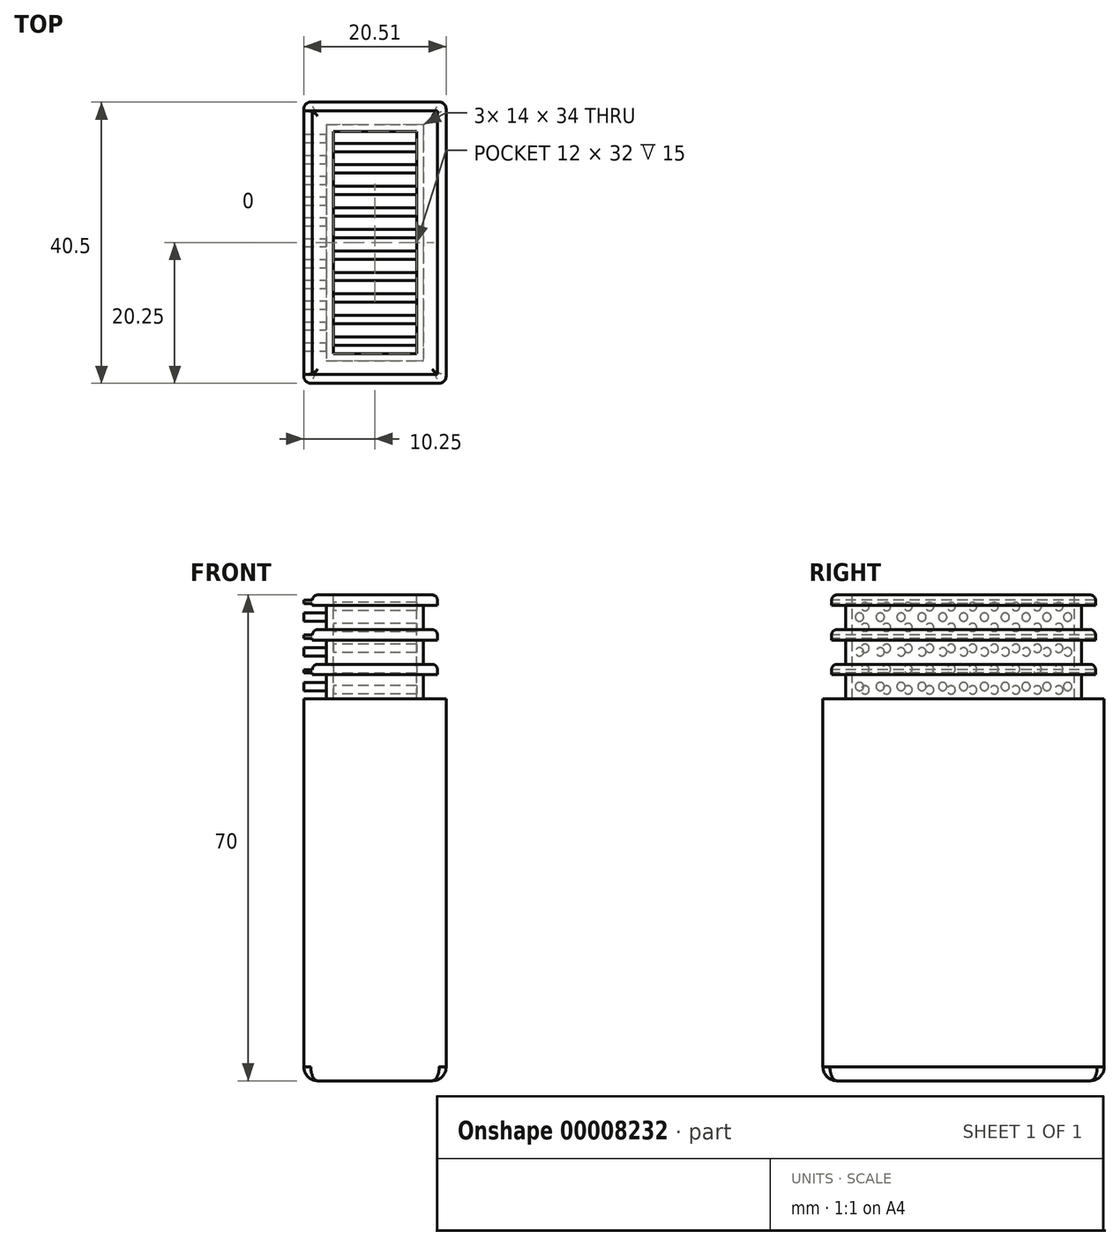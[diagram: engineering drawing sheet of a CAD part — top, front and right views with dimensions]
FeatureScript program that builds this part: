
annotation { "Feature Type Name" : "Feature", "Feature Type Description" : "" }
export const myFeature = defineFeature(function(context is Context, id is Id, definition is map)
    precondition{}
    {
        {
            var Q0;
            Q0=qCreatedBy(makeId("Top.planeOp"),FACE);
            var sketch = newSketch(context, id + "F0", { "sketchPlane" : qUnion([Q0])});
            skLineSegment(sketch, "E0.rect.bottom", {"start": v(10.25, -20.25) * mm, "end": v(-10.25, -20.25) * mm});
            skLineSegment(sketch, "E0.rect.top", {"start": v(10.25, 20.25) * mm, "end": v(-10.25, 20.25) * mm});
            skLineSegment(sketch, "E0.rect.left", {"start": v(10.25, -20.25) * mm, "end": v(10.25, 20.25) * mm});
            skLineSegment(sketch, "E0.rect.right", {"start": v(-10.25, -20.25) * mm, "end": v(-10.25, 20.25) * mm});
            skPoint(sketch, "E0.rect.middle", {"position": v(0, 0) * mm});
            skSolve(sketch);
        }
        {
            var Q0;
            Q0=makeQuery(id+"F0.imprint","IMPRINT",FACE,{"disambiguationData":[TD([[makeQuery(id+"F0.imprint","IMPRINT",EDGE,{"derivedFrom":sQuery(id+"F0.wireOp",EDGE,"E0.rect.bottom")}),-1.0]])]});
            extrude(context, id + "F1", {"entities" : qUnion([Q0]), "depth" : 53 * mm});
        }
        {
            var Q0;
            Q0=makeQuery(id+"F1.opExtrude","CAP_FACE",FACE,{"disambiguationData":[OSD([sQuery(id+"F0.wireOp",EDGE,"E0.rect.bottom"),sQuery(id+"F0.wireOp",EDGE,"E0.rect.top"),sQuery(id+"F0.wireOp",EDGE,"E0.rect.left"),sQuery(id+"F0.wireOp",EDGE,"E0.rect.right")])],"isStart":false});
            var sketch = newSketch(context, id + "F2", { "sketchPlane" : qUnion([Q0])});
            skLineSegment(sketch, "E1.bottom", {"start": v(-7, 17) * mm, "end": v(7, 17) * mm});
            skLineSegment(sketch, "E1.top", {"start": v(-7, -17) * mm, "end": v(7, -17) * mm});
            skLineSegment(sketch, "E1.left", {"start": v(-7, 17) * mm, "end": v(-7, -17) * mm});
            skLineSegment(sketch, "E1.right", {"start": v(7, 17) * mm, "end": v(7, -17) * mm});
            skSolve(sketch);
        }
        {
            var Q0;
            Q0 = qSketchRegion(id + "F2", true);
            extrude(context, id + "F3", {"entities" : qUnion([Q0]), "operationType" : NewBodyOperationType.ADD, "depth" : 3.5 * mm});
        }
        {
            var Q0;
            Q0=makeQuery(id+"F3.opExtrude","CAP_FACE",FACE,{"disambiguationData":[OSD([sQuery(id+"F2.wireOp",EDGE,"E1.bottom"),sQuery(id+"F2.wireOp",EDGE,"E1.top"),sQuery(id+"F2.wireOp",EDGE,"E1.left"),sQuery(id+"F2.wireOp",EDGE,"E1.right")])],"isStart":false});
            var sketch = newSketch(context, id + "F4", { "sketchPlane" : qUnion([Q0])});
            skLineSegment(sketch, "E2.bottom", {"start": v(-9, 19) * mm, "end": v(9, 19) * mm});
            skLineSegment(sketch, "E2.top", {"start": v(-9, -19) * mm, "end": v(9, -19) * mm});
            skLineSegment(sketch, "E2.left", {"start": v(-9, 19) * mm, "end": v(-9, -19) * mm});
            skLineSegment(sketch, "E2.right", {"start": v(9, 19) * mm, "end": v(9, -19) * mm});
            skSolve(sketch);
        }
        {
            var Q0;
            Q0 = qSketchRegion(id + "F4", true);
            extrude(context, id + "F5", {"entities" : qUnion([Q0]), "operationType" : NewBodyOperationType.ADD, "depth" : 1.5 * mm});
        }
        {
            var Q0;
            Q0=makeQuery(id+"F5.opExtrude","CAP_FACE",FACE,{"disambiguationData":[OSD([sQuery(id+"F4.wireOp",EDGE,"E2.bottom"),sQuery(id+"F4.wireOp",EDGE,"E2.top"),sQuery(id+"F4.wireOp",EDGE,"E2.left"),sQuery(id+"F4.wireOp",EDGE,"E2.right")])],"isStart":false});
            fillet(context, id + "F6", {"entities" : qUnion([Q0]), "radius" : 0.75 * mm, "tangentPropagation" : true, "allowEdgeOverflow" : false});
        }
        {
            var Q0;
            Q0=makeQuery(id+"F5.opExtrude","CAP_FACE",FACE,{"disambiguationData":[OSD([sQuery(id+"F4.wireOp",EDGE,"E2.bottom"),sQuery(id+"F4.wireOp",EDGE,"E2.top"),sQuery(id+"F4.wireOp",EDGE,"E2.left"),sQuery(id+"F4.wireOp",EDGE,"E2.right")])],"isStart":false});
            var sketch = newSketch(context, id + "F7", { "sketchPlane" : qUnion([Q0])});
            skLineSegment(sketch, "E3.rect.bottom", {"start": v(-7, -17) * mm, "end": v(7, -17) * mm});
            skLineSegment(sketch, "E3.rect.top", {"start": v(-7, 17) * mm, "end": v(7, 17) * mm});
            skLineSegment(sketch, "E3.rect.left", {"start": v(-7, -17) * mm, "end": v(-7, 17) * mm});
            skLineSegment(sketch, "E3.rect.right", {"start": v(7, -17) * mm, "end": v(7, 17) * mm});
            skPoint(sketch, "E3.rect.middle", {"position": v(0, 0) * mm});
            skSolve(sketch);
        }
        {
            var Q0;
            Q0 = qSketchRegion(id + "F7", true);
            extrude(context, id + "F8", {"entities" : qUnion([Q0]), "operationType" : NewBodyOperationType.ADD, "depth" : 3.5 * mm});
        }
        {
            var Q0;
            Q0=makeQuery(id+"F8.opExtrude","CAP_FACE",FACE,{"disambiguationData":[OSD([sQuery(id+"F7.wireOp",EDGE,"E3.rect.bottom"),sQuery(id+"F7.wireOp",EDGE,"E3.rect.top"),sQuery(id+"F7.wireOp",EDGE,"E3.rect.left"),sQuery(id+"F7.wireOp",EDGE,"E3.rect.right")])],"isStart":false});
            var sketch = newSketch(context, id + "F9", { "sketchPlane" : qUnion([Q0])});
            skLineSegment(sketch, "E4.bottom", {"start": v(-9, 19) * mm, "end": v(9, 19) * mm});
            skLineSegment(sketch, "E4.top", {"start": v(-9, -19) * mm, "end": v(9, -19) * mm});
            skLineSegment(sketch, "E4.left", {"start": v(-9, 19) * mm, "end": v(-9, -19) * mm});
            skLineSegment(sketch, "E4.right", {"start": v(9, 19) * mm, "end": v(9, -19) * mm});
            skSolve(sketch);
        }
        {
            var Q0;
            Q0 = qSketchRegion(id + "F9", true);
            extrude(context, id + "F10", {"entities" : qUnion([Q0]), "operationType" : NewBodyOperationType.ADD, "depth" : 1.5 * mm});
        }
        {
            var Q0;
            Q0=makeQuery(id+"F10.opExtrude","CAP_FACE",FACE,{"disambiguationData":[OSD([sQuery(id+"F9.wireOp",EDGE,"E4.bottom"),sQuery(id+"F9.wireOp",EDGE,"E4.top"),sQuery(id+"F9.wireOp",EDGE,"E4.left"),sQuery(id+"F9.wireOp",EDGE,"E4.right")])],"isStart":false});
            var sketch = newSketch(context, id + "F11", { "sketchPlane" : qUnion([Q0])});
            skLineSegment(sketch, "E5.bottom", {"start": v(-7, 17) * mm, "end": v(7, 17) * mm});
            skLineSegment(sketch, "E5.top", {"start": v(-7, -17) * mm, "end": v(7, -17) * mm});
            skLineSegment(sketch, "E5.left", {"start": v(-7, 17) * mm, "end": v(-7, -17) * mm});
            skLineSegment(sketch, "E5.right", {"start": v(7, 17) * mm, "end": v(7, -17) * mm});
            skSolve(sketch);
        }
        {
            var Q0;
            Q0 = qSketchRegion(id + "F11", true);
            extrude(context, id + "F12", {"entities" : qUnion([Q0]), "operationType" : NewBodyOperationType.ADD, "depth" : 3.5 * mm});
        }
        {
            var Q0;
            Q0=makeQuery(id+"F12.opExtrude","CAP_FACE",FACE,{"disambiguationData":[OSD([sQuery(id+"F11.wireOp",EDGE,"E5.bottom"),sQuery(id+"F11.wireOp",EDGE,"E5.top"),sQuery(id+"F11.wireOp",EDGE,"E5.left"),sQuery(id+"F11.wireOp",EDGE,"E5.right")])],"isStart":false});
            var sketch = newSketch(context, id + "F13", { "sketchPlane" : qUnion([Q0])});
            skLineSegment(sketch, "E6.bottom", {"start": v(-9, 19) * mm, "end": v(9, 19) * mm});
            skLineSegment(sketch, "E6.top", {"start": v(-9, -19) * mm, "end": v(9, -19) * mm});
            skLineSegment(sketch, "E6.left", {"start": v(-9, 19) * mm, "end": v(-9, -19) * mm});
            skLineSegment(sketch, "E6.right", {"start": v(9, 19) * mm, "end": v(9, -19) * mm});
            skSolve(sketch);
        }
        {
            var Q0;
            Q0=makeQuery(id+"F13.imprint","IMPRINT",FACE,{"disambiguationData":[TD([[makeQuery(id+"F13.imprint","IMPRINT",EDGE,{"derivedFrom":sQuery(id+"F13.wireOp",EDGE,"E6.bottom")}),-1.0]])]});
            var Q1;
            Q1=makeQuery(id+"F13.imprint","IMPRINT",FACE,{"disambiguationData":[TD([[makeQuery(id+"F13.imprint","IMPRINT",EDGE,{"derivedFrom":makeQuery(id+"F12.opExtrude","CAP_EDGE",EDGE,{"disambiguationData":[OSD([sQuery(id+"F11.wireOp",EDGE,"E5.bottom")])],"isStart":false})}),-1.0]])]});
            extrude(context, id + "F14", {"entities" : qUnion([Q0, Q1]), "operationType" : NewBodyOperationType.ADD, "depth" : 1.5 * mm});
        }
        {
            var Q0;
            Q0=makeQuery(id+"F10.opExtrude","CAP_EDGE",EDGE,{"disambiguationData":[OSD([sQuery(id+"F9.wireOp",EDGE,"E4.bottom")])],"isStart":false});
            var Q1;
            Q1=makeQuery(id+"F10.opExtrude","CAP_EDGE",EDGE,{"disambiguationData":[OSD([sQuery(id+"F9.wireOp",EDGE,"E4.left")])],"isStart":false});
            var Q2;
            Q2=makeQuery(id+"F10.opExtrude","CAP_EDGE",EDGE,{"disambiguationData":[OSD([sQuery(id+"F9.wireOp",EDGE,"E4.right")])],"isStart":false});
            var Q3;
            Q3=makeQuery(id+"F10.opExtrude","CAP_EDGE",EDGE,{"disambiguationData":[OSD([sQuery(id+"F9.wireOp",EDGE,"E4.top")])],"isStart":false});
            fillet(context, id + "F15", {"entities" : qUnion([Q0, Q1, Q2, Q3]), "radius" : 0.75 * mm, "tangentPropagation" : true, "allowEdgeOverflow" : false});
        }
        {
            var Q0;
            Q0=makeQuery(id+"F14.opExtrude","CAP_EDGE",EDGE,{"disambiguationData":[OSD([sQuery(id+"F13.wireOp",EDGE,"E6.left")])],"isStart":false});
            var Q1;
            Q1=makeQuery(id+"F14.opExtrude","CAP_EDGE",EDGE,{"disambiguationData":[OSD([sQuery(id+"F13.wireOp",EDGE,"E6.top")])],"isStart":false});
            var Q2;
            Q2=makeQuery(id+"F14.opExtrude","CAP_EDGE",EDGE,{"disambiguationData":[OSD([sQuery(id+"F13.wireOp",EDGE,"E6.right")])],"isStart":false});
            var Q3;
            Q3=makeQuery(id+"F14.opExtrude","CAP_EDGE",EDGE,{"disambiguationData":[OSD([sQuery(id+"F13.wireOp",EDGE,"E6.bottom")])],"isStart":false});
            fillet(context, id + "F16", {"entities" : qUnion([Q0, Q1, Q2, Q3]), "radius" : 0.75 * mm, "tangentPropagation" : true, "allowEdgeOverflow" : false});
        }
        {
            var Q0;
            Q0=makeQuery(id+"F14.opExtrude","CAP_FACE",FACE,{"disambiguationData":[OSD([sQuery(id+"F13.wireOp",EDGE,"E6.bottom"),sQuery(id+"F13.wireOp",EDGE,"E6.top"),sQuery(id+"F13.wireOp",EDGE,"E6.left"),sQuery(id+"F13.wireOp",EDGE,"E6.right")])],"isStart":false});
            var sketch = newSketch(context, id + "F17", { "sketchPlane" : qUnion([Q0])});
            skLineSegment(sketch, "E7.bottom", {"start": v(-6, 16) * mm, "end": v(6, 16) * mm});
            skLineSegment(sketch, "E7.top", {"start": v(-6, -16) * mm, "end": v(6, -16) * mm});
            skLineSegment(sketch, "E7.left", {"start": v(-6, 16) * mm, "end": v(-6, -16) * mm});
            skLineSegment(sketch, "E7.right", {"start": v(6, 16) * mm, "end": v(6, -16) * mm});
            skSolve(sketch);
        }
        {
            var Q0;
            Q0=makeQuery(id+"F17.imprint","IMPRINT",FACE,{"disambiguationData":[TD([[makeQuery(id+"F17.imprint","IMPRINT",EDGE,{"derivedFrom":sQuery(id+"F17.wireOp",EDGE,"E7.bottom")}),-1.0]])]});
            var Q1;
            Q1=makeQuery(id+"F1.opExtrude","CAP_FACE",FACE,{"disambiguationData":[OSD([sQuery(id+"F0.wireOp",EDGE,"E0.rect.bottom"),sQuery(id+"F0.wireOp",EDGE,"E0.rect.top"),sQuery(id+"F0.wireOp",EDGE,"E0.rect.left"),sQuery(id+"F0.wireOp",EDGE,"E0.rect.right")])],"isStart":false});
            extrude(context, id + "F18", {"entities" : qUnion([Q0]), "operationType" : NewBodyOperationType.REMOVE, "oppositeDirection" : true, "endBoundEntity" : qUnion([Q1]), "depth" : 15 * mm});
        }
        {
            var Q0;
            Q0=makeQuery(id+"F1.opExtrude","SWEPT_EDGE",EDGE,{"disambiguationData":[OSD([sQuery(id+"F0.wireOp",EDGE,"E0.rect.bottom"),sQuery(id+"F0.wireOp",EDGE,"E0.rect.left")])]});
            var Q1;
            Q1=makeQuery(id+"F1.opExtrude","SWEPT_EDGE",EDGE,{"disambiguationData":[OSD([sQuery(id+"F0.wireOp",EDGE,"E0.rect.top"),sQuery(id+"F0.wireOp",EDGE,"E0.rect.left")])]});
            var Q2;
            Q2=makeQuery(id+"F1.opExtrude","SWEPT_EDGE",EDGE,{"disambiguationData":[OSD([sQuery(id+"F0.wireOp",EDGE,"E0.rect.top"),sQuery(id+"F0.wireOp",EDGE,"E0.rect.right")])]});
            var Q3;
            Q3=makeQuery(id+"F1.opExtrude","SWEPT_EDGE",EDGE,{"disambiguationData":[OSD([sQuery(id+"F0.wireOp",EDGE,"E0.rect.bottom"),sQuery(id+"F0.wireOp",EDGE,"E0.rect.right")])]});
            fillet(context, id + "F19", {"entities" : qUnion([Q0, Q1, Q2, Q3]), "radius" : 1 * mm, "tangentPropagation" : true, "allowEdgeOverflow" : false});
        }
        {
            var Q0;
            Q0=makeQuery(id+"F1.opExtrude","CAP_FACE",FACE,{"disambiguationData":[OSD([sQuery(id+"F0.wireOp",EDGE,"E0.rect.bottom"),sQuery(id+"F0.wireOp",EDGE,"E0.rect.top"),sQuery(id+"F0.wireOp",EDGE,"E0.rect.left"),sQuery(id+"F0.wireOp",EDGE,"E0.rect.right")])],"isStart":true});
            var sketch = newSketch(context, id + "F20", { "sketchPlane" : qUnion([Q0])});
            skLineSegment(sketch, "E8.bottom", {"start": v(-7.25, 17.25) * mm, "end": v(-4.75, 17.25) * mm});
            skLineSegment(sketch, "E8.top", {"start": v(-7.25, 14.25) * mm, "end": v(-4.75, 14.25) * mm});
            skLineSegment(sketch, "E8.left", {"start": v(-7.25, 17.25) * mm, "end": v(-7.25, 14.25) * mm});
            skLineSegment(sketch, "E8.right", {"start": v(-4.75, 17.25) * mm, "end": v(-4.75, 14.25) * mm});
            skLineSegment(sketch, "E9.1.0.0", {"start": v(-3.25, 17.25) * mm, "end": v(-0.75, 17.25) * mm});
            skLineSegment(sketch, "E9.1.0.1", {"start": v(-0.75, 17.25) * mm, "end": v(-0.75, 14.25) * mm});
            skLineSegment(sketch, "E9.1.0.2", {"start": v(-3.25, 17.25) * mm, "end": v(-3.25, 14.25) * mm});
            skLineSegment(sketch, "E9.1.0.3", {"start": v(-3.25, 14.25) * mm, "end": v(-0.75, 14.25) * mm});
            skLineSegment(sketch, "E9.2.0.0", {"start": v(0.75, 17.25) * mm, "end": v(3.25, 17.25) * mm});
            skLineSegment(sketch, "E9.2.0.1", {"start": v(3.25, 17.25) * mm, "end": v(3.25, 14.25) * mm});
            skLineSegment(sketch, "E9.2.0.2", {"start": v(0.75, 17.25) * mm, "end": v(0.75, 14.25) * mm});
            skLineSegment(sketch, "E9.2.0.3", {"start": v(0.75, 14.25) * mm, "end": v(3.25, 14.25) * mm});
            skLineSegment(sketch, "E9.3.0.0", {"start": v(4.75, 17.25) * mm, "end": v(7.25, 17.25) * mm});
            skLineSegment(sketch, "E9.3.0.1", {"start": v(7.25, 17.25) * mm, "end": v(7.25, 14.25) * mm});
            skLineSegment(sketch, "E9.3.0.2", {"start": v(4.75, 17.25) * mm, "end": v(4.75, 14.25) * mm});
            skLineSegment(sketch, "E9.3.0.3", {"start": v(4.75, 14.25) * mm, "end": v(7.25, 14.25) * mm});
            skLineSegment(sketch, "E9.direction1", {"start": v(-7.25, 17.25) * mm, "end": v(-3.25, 17.25) * mm, "construction": true});
            skLineSegment(sketch, "E10.1.0.0", {"start": v(-7.24, 12.75) * mm, "end": v(-7.24, 9.75) * mm});
            skLineSegment(sketch, "E10.1.0.1", {"start": v(-3.24, 12.75) * mm, "end": v(-3.24, 9.75) * mm});
            skLineSegment(sketch, "E10.1.0.2", {"start": v(-3.24, 9.75) * mm, "end": v(-0.74, 9.75) * mm});
            skLineSegment(sketch, "E10.1.0.3", {"start": v(4.76, 9.75) * mm, "end": v(7.26, 9.75) * mm});
            skLineSegment(sketch, "E10.1.0.4", {"start": v(-7.24, 9.75) * mm, "end": v(-4.74, 9.75) * mm});
            skLineSegment(sketch, "E10.1.0.5", {"start": v(-7.24, 12.75) * mm, "end": v(-4.74, 12.75) * mm});
            skLineSegment(sketch, "E10.1.0.6", {"start": v(4.76, 12.75) * mm, "end": v(4.76, 9.75) * mm});
            skLineSegment(sketch, "E10.1.0.7", {"start": v(-0.74, 12.75) * mm, "end": v(-0.74, 9.75) * mm});
            skLineSegment(sketch, "E10.1.0.8", {"start": v(-7.24, 12.75) * mm, "end": v(-3.24, 12.75) * mm, "construction": true});
            skLineSegment(sketch, "E10.1.0.9", {"start": v(0.76, 9.75) * mm, "end": v(3.26, 9.75) * mm});
            skLineSegment(sketch, "E10.1.0.10", {"start": v(4.76, 12.75) * mm, "end": v(7.26, 12.75) * mm});
            skLineSegment(sketch, "E10.1.0.11", {"start": v(0.76, 12.75) * mm, "end": v(3.26, 12.75) * mm});
            skLineSegment(sketch, "E10.1.0.12", {"start": v(3.26, 12.75) * mm, "end": v(3.26, 9.75) * mm});
            skLineSegment(sketch, "E10.1.0.13", {"start": v(7.26, 12.75) * mm, "end": v(7.26, 9.75) * mm});
            skLineSegment(sketch, "E10.1.0.14", {"start": v(0.76, 12.75) * mm, "end": v(0.76, 9.75) * mm});
            skLineSegment(sketch, "E10.1.0.15", {"start": v(-3.24, 12.75) * mm, "end": v(-0.74, 12.75) * mm});
            skLineSegment(sketch, "E10.1.0.16", {"start": v(-4.74, 12.75) * mm, "end": v(-4.74, 9.75) * mm});
            skLineSegment(sketch, "E10.2.0.0", {"start": v(-7.22, 8.25) * mm, "end": v(-7.22, 5.25) * mm});
            skLineSegment(sketch, "E10.2.0.1", {"start": v(-3.22, 8.25) * mm, "end": v(-3.22, 5.25) * mm});
            skLineSegment(sketch, "E10.2.0.2", {"start": v(-3.22, 5.25) * mm, "end": v(-0.72, 5.25) * mm});
            skLineSegment(sketch, "E10.2.0.3", {"start": v(4.78, 5.25) * mm, "end": v(7.28, 5.25) * mm});
            skLineSegment(sketch, "E10.2.0.4", {"start": v(-7.22, 5.25) * mm, "end": v(-4.72, 5.25) * mm});
            skLineSegment(sketch, "E10.2.0.5", {"start": v(-7.22, 8.25) * mm, "end": v(-4.72, 8.25) * mm});
            skLineSegment(sketch, "E10.2.0.6", {"start": v(4.78, 8.25) * mm, "end": v(4.78, 5.25) * mm});
            skLineSegment(sketch, "E10.2.0.7", {"start": v(-0.72, 8.25) * mm, "end": v(-0.72, 5.25) * mm});
            skLineSegment(sketch, "E10.2.0.8", {"start": v(-7.22, 8.25) * mm, "end": v(-3.22, 8.25) * mm, "construction": true});
            skLineSegment(sketch, "E10.2.0.9", {"start": v(0.78, 5.25) * mm, "end": v(3.28, 5.25) * mm});
            skLineSegment(sketch, "E10.2.0.10", {"start": v(4.78, 8.25) * mm, "end": v(7.28, 8.25) * mm});
            skLineSegment(sketch, "E10.2.0.11", {"start": v(0.78, 8.25) * mm, "end": v(3.28, 8.25) * mm});
            skLineSegment(sketch, "E10.2.0.12", {"start": v(3.28, 8.25) * mm, "end": v(3.28, 5.25) * mm});
            skLineSegment(sketch, "E10.2.0.13", {"start": v(7.28, 8.25) * mm, "end": v(7.28, 5.25) * mm});
            skLineSegment(sketch, "E10.2.0.14", {"start": v(0.78, 8.25) * mm, "end": v(0.78, 5.25) * mm});
            skLineSegment(sketch, "E10.2.0.15", {"start": v(-3.22, 8.25) * mm, "end": v(-0.72, 8.25) * mm});
            skLineSegment(sketch, "E10.2.0.16", {"start": v(-4.72, 8.25) * mm, "end": v(-4.72, 5.25) * mm});
            skLineSegment(sketch, "E10.3.0.0", {"start": v(-7.21, 3.75) * mm, "end": v(-7.21, 0.75) * mm});
            skLineSegment(sketch, "E10.3.0.1", {"start": v(-3.21, 3.75) * mm, "end": v(-3.21, 0.75) * mm});
            skLineSegment(sketch, "E10.3.0.2", {"start": v(-3.21, 0.75) * mm, "end": v(-0.71, 0.75) * mm});
            skLineSegment(sketch, "E10.3.0.3", {"start": v(4.79, 0.75) * mm, "end": v(7.29, 0.75) * mm});
            skLineSegment(sketch, "E10.3.0.4", {"start": v(-7.21, 0.75) * mm, "end": v(-4.71, 0.75) * mm});
            skLineSegment(sketch, "E10.3.0.5", {"start": v(-7.21, 3.75) * mm, "end": v(-4.71, 3.75) * mm});
            skLineSegment(sketch, "E10.3.0.6", {"start": v(4.79, 3.75) * mm, "end": v(4.79, 0.75) * mm});
            skLineSegment(sketch, "E10.3.0.7", {"start": v(-0.71, 3.75) * mm, "end": v(-0.71, 0.75) * mm});
            skLineSegment(sketch, "E10.3.0.8", {"start": v(-7.21, 3.75) * mm, "end": v(-3.21, 3.75) * mm, "construction": true});
            skLineSegment(sketch, "E10.3.0.9", {"start": v(0.79, 0.75) * mm, "end": v(3.29, 0.75) * mm});
            skLineSegment(sketch, "E10.3.0.10", {"start": v(4.79, 3.75) * mm, "end": v(7.29, 3.75) * mm});
            skLineSegment(sketch, "E10.3.0.11", {"start": v(0.79, 3.75) * mm, "end": v(3.29, 3.75) * mm});
            skLineSegment(sketch, "E10.3.0.12", {"start": v(3.29, 3.75) * mm, "end": v(3.29, 0.75) * mm});
            skLineSegment(sketch, "E10.3.0.13", {"start": v(7.29, 3.75) * mm, "end": v(7.29, 0.75) * mm});
            skLineSegment(sketch, "E10.3.0.14", {"start": v(0.79, 3.75) * mm, "end": v(0.79, 0.75) * mm});
            skLineSegment(sketch, "E10.3.0.15", {"start": v(-3.21, 3.75) * mm, "end": v(-0.71, 3.75) * mm});
            skLineSegment(sketch, "E10.3.0.16", {"start": v(-4.71, 3.75) * mm, "end": v(-4.71, 0.75) * mm});
            skLineSegment(sketch, "E10.4.0.0", {"start": v(-7.2, -0.75) * mm, "end": v(-7.2, -3.75) * mm});
            skLineSegment(sketch, "E10.4.0.1", {"start": v(-3.2, -0.75) * mm, "end": v(-3.2, -3.75) * mm});
            skLineSegment(sketch, "E10.4.0.2", {"start": v(-3.2, -3.75) * mm, "end": v(-0.7, -3.75) * mm});
            skLineSegment(sketch, "E10.4.0.3", {"start": v(4.8, -3.75) * mm, "end": v(7.3, -3.75) * mm});
            skLineSegment(sketch, "E10.4.0.4", {"start": v(-7.2, -3.75) * mm, "end": v(-4.7, -3.75) * mm});
            skLineSegment(sketch, "E10.4.0.5", {"start": v(-7.2, -0.75) * mm, "end": v(-4.7, -0.75) * mm});
            skLineSegment(sketch, "E10.4.0.6", {"start": v(4.8, -0.75) * mm, "end": v(4.8, -3.75) * mm});
            skLineSegment(sketch, "E10.4.0.7", {"start": v(-0.7, -0.75) * mm, "end": v(-0.7, -3.75) * mm});
            skLineSegment(sketch, "E10.4.0.8", {"start": v(-7.2, -0.75) * mm, "end": v(-3.2, -0.75) * mm, "construction": true});
            skLineSegment(sketch, "E10.4.0.9", {"start": v(0.8, -3.75) * mm, "end": v(3.3, -3.75) * mm});
            skLineSegment(sketch, "E10.4.0.10", {"start": v(4.8, -0.75) * mm, "end": v(7.3, -0.75) * mm});
            skLineSegment(sketch, "E10.4.0.11", {"start": v(0.8, -0.75) * mm, "end": v(3.3, -0.75) * mm});
            skLineSegment(sketch, "E10.4.0.12", {"start": v(3.3, -0.75) * mm, "end": v(3.3, -3.75) * mm});
            skLineSegment(sketch, "E10.4.0.13", {"start": v(7.3, -0.75) * mm, "end": v(7.3, -3.75) * mm});
            skLineSegment(sketch, "E10.4.0.14", {"start": v(0.8, -0.75) * mm, "end": v(0.8, -3.75) * mm});
            skLineSegment(sketch, "E10.4.0.15", {"start": v(-3.2, -0.75) * mm, "end": v(-0.7, -0.75) * mm});
            skLineSegment(sketch, "E10.4.0.16", {"start": v(-4.7, -0.75) * mm, "end": v(-4.7, -3.75) * mm});
            skLineSegment(sketch, "E10.5.0.0", {"start": v(-7.18, -5.25) * mm, "end": v(-7.18, -8.25) * mm});
            skLineSegment(sketch, "E10.5.0.1", {"start": v(-3.18, -5.25) * mm, "end": v(-3.18, -8.25) * mm});
            skLineSegment(sketch, "E10.5.0.2", {"start": v(-3.18, -8.25) * mm, "end": v(-0.68, -8.25) * mm});
            skLineSegment(sketch, "E10.5.0.3", {"start": v(4.82, -8.25) * mm, "end": v(7.32, -8.25) * mm});
            skLineSegment(sketch, "E10.5.0.4", {"start": v(-7.18, -8.25) * mm, "end": v(-4.68, -8.25) * mm});
            skLineSegment(sketch, "E10.5.0.5", {"start": v(-7.18, -5.25) * mm, "end": v(-4.68, -5.25) * mm});
            skLineSegment(sketch, "E10.5.0.6", {"start": v(4.82, -5.25) * mm, "end": v(4.82, -8.25) * mm});
            skLineSegment(sketch, "E10.5.0.7", {"start": v(-0.68, -5.25) * mm, "end": v(-0.68, -8.25) * mm});
            skLineSegment(sketch, "E10.5.0.8", {"start": v(-7.18, -5.25) * mm, "end": v(-3.18, -5.25) * mm, "construction": true});
            skLineSegment(sketch, "E10.5.0.9", {"start": v(0.82, -8.25) * mm, "end": v(3.32, -8.25) * mm});
            skLineSegment(sketch, "E10.5.0.10", {"start": v(4.82, -5.25) * mm, "end": v(7.32, -5.25) * mm});
            skLineSegment(sketch, "E10.5.0.11", {"start": v(0.82, -5.25) * mm, "end": v(3.32, -5.25) * mm});
            skLineSegment(sketch, "E10.5.0.12", {"start": v(3.32, -5.25) * mm, "end": v(3.32, -8.25) * mm});
            skLineSegment(sketch, "E10.5.0.13", {"start": v(7.32, -5.25) * mm, "end": v(7.32, -8.25) * mm});
            skLineSegment(sketch, "E10.5.0.14", {"start": v(0.82, -5.25) * mm, "end": v(0.82, -8.25) * mm});
            skLineSegment(sketch, "E10.5.0.15", {"start": v(-3.18, -5.25) * mm, "end": v(-0.68, -5.25) * mm});
            skLineSegment(sketch, "E10.5.0.16", {"start": v(-4.68, -5.25) * mm, "end": v(-4.68, -8.25) * mm});
            skLineSegment(sketch, "E10.6.0.0", {"start": v(-7.17, -9.75) * mm, "end": v(-7.17, -12.75) * mm});
            skLineSegment(sketch, "E10.6.0.1", {"start": v(-3.17, -9.75) * mm, "end": v(-3.17, -12.75) * mm});
            skLineSegment(sketch, "E10.6.0.2", {"start": v(-3.17, -12.75) * mm, "end": v(-0.67, -12.75) * mm});
            skLineSegment(sketch, "E10.6.0.3", {"start": v(4.83, -12.75) * mm, "end": v(7.33, -12.75) * mm});
            skLineSegment(sketch, "E10.6.0.4", {"start": v(-7.17, -12.75) * mm, "end": v(-4.67, -12.75) * mm});
            skLineSegment(sketch, "E10.6.0.5", {"start": v(-7.17, -9.75) * mm, "end": v(-4.67, -9.75) * mm});
            skLineSegment(sketch, "E10.6.0.6", {"start": v(4.83, -9.75) * mm, "end": v(4.83, -12.75) * mm});
            skLineSegment(sketch, "E10.6.0.7", {"start": v(-0.67, -9.75) * mm, "end": v(-0.67, -12.75) * mm});
            skLineSegment(sketch, "E10.6.0.8", {"start": v(-7.17, -9.75) * mm, "end": v(-3.17, -9.75) * mm, "construction": true});
            skLineSegment(sketch, "E10.6.0.9", {"start": v(0.83, -12.75) * mm, "end": v(3.33, -12.75) * mm});
            skLineSegment(sketch, "E10.6.0.10", {"start": v(4.83, -9.75) * mm, "end": v(7.33, -9.75) * mm});
            skLineSegment(sketch, "E10.6.0.11", {"start": v(0.83, -9.75) * mm, "end": v(3.33, -9.75) * mm});
            skLineSegment(sketch, "E10.6.0.12", {"start": v(3.33, -9.75) * mm, "end": v(3.33, -12.75) * mm});
            skLineSegment(sketch, "E10.6.0.13", {"start": v(7.33, -9.75) * mm, "end": v(7.33, -12.75) * mm});
            skLineSegment(sketch, "E10.6.0.14", {"start": v(0.83, -9.75) * mm, "end": v(0.83, -12.75) * mm});
            skLineSegment(sketch, "E10.6.0.15", {"start": v(-3.17, -9.75) * mm, "end": v(-0.67, -9.75) * mm});
            skLineSegment(sketch, "E10.6.0.16", {"start": v(-4.67, -9.75) * mm, "end": v(-4.67, -12.75) * mm});
            skLineSegment(sketch, "E10.7.0.0", {"start": v(-7.16, -14.25) * mm, "end": v(-7.16, -17.25) * mm});
            skLineSegment(sketch, "E10.7.0.1", {"start": v(-3.16, -14.25) * mm, "end": v(-3.16, -17.25) * mm});
            skLineSegment(sketch, "E10.7.0.2", {"start": v(-3.16, -17.25) * mm, "end": v(-0.66, -17.25) * mm});
            skLineSegment(sketch, "E10.7.0.3", {"start": v(4.84, -17.25) * mm, "end": v(7.34, -17.25) * mm});
            skLineSegment(sketch, "E10.7.0.4", {"start": v(-7.16, -17.25) * mm, "end": v(-4.66, -17.25) * mm});
            skLineSegment(sketch, "E10.7.0.5", {"start": v(-7.16, -14.25) * mm, "end": v(-4.66, -14.25) * mm});
            skLineSegment(sketch, "E10.7.0.6", {"start": v(4.84, -14.25) * mm, "end": v(4.84, -17.25) * mm});
            skLineSegment(sketch, "E10.7.0.7", {"start": v(-0.66, -14.25) * mm, "end": v(-0.66, -17.25) * mm});
            skLineSegment(sketch, "E10.7.0.8", {"start": v(-7.16, -14.25) * mm, "end": v(-3.16, -14.25) * mm, "construction": true});
            skLineSegment(sketch, "E10.7.0.9", {"start": v(0.84, -17.25) * mm, "end": v(3.34, -17.25) * mm});
            skLineSegment(sketch, "E10.7.0.10", {"start": v(4.84, -14.25) * mm, "end": v(7.34, -14.25) * mm});
            skLineSegment(sketch, "E10.7.0.11", {"start": v(0.84, -14.25) * mm, "end": v(3.34, -14.25) * mm});
            skLineSegment(sketch, "E10.7.0.12", {"start": v(3.34, -14.25) * mm, "end": v(3.34, -17.25) * mm});
            skLineSegment(sketch, "E10.7.0.13", {"start": v(7.34, -14.25) * mm, "end": v(7.34, -17.25) * mm});
            skLineSegment(sketch, "E10.7.0.14", {"start": v(0.84, -14.25) * mm, "end": v(0.84, -17.25) * mm});
            skLineSegment(sketch, "E10.7.0.15", {"start": v(-3.16, -14.25) * mm, "end": v(-0.66, -14.25) * mm});
            skLineSegment(sketch, "E10.7.0.16", {"start": v(-4.66, -14.25) * mm, "end": v(-4.66, -17.25) * mm});
            skLineSegment(sketch, "E10.direction1", {"start": v(-7.25, 14.25) * mm, "end": v(-7.24, 9.75) * mm, "construction": true});
            skSolve(sketch);
        }
        {
            var Q0;
            Q0=makeQuery(id+"F1.opExtrude","CAP_FACE",FACE,{"disambiguationData":[OSD([sQuery(id+"F0.wireOp",EDGE,"E0.rect.bottom"),sQuery(id+"F0.wireOp",EDGE,"E0.rect.top"),sQuery(id+"F0.wireOp",EDGE,"E0.rect.left"),sQuery(id+"F0.wireOp",EDGE,"E0.rect.right")])],"isStart":true});
            var sketch = newSketch(context, id + "F21", { "sketchPlane" : qUnion([Q0])});
            skLineSegment(sketch, "E11.bottom", {"start": v(-10.24, 20.25) * mm, "end": v(10.26, 20.25) * mm});
            skLineSegment(sketch, "E11.top", {"start": v(-10.24, -20.25) * mm, "end": v(10.26, -20.25) * mm});
            skLineSegment(sketch, "E11.left", {"start": v(-10.24, 20.25) * mm, "end": v(-10.24, -20.25) * mm});
            skLineSegment(sketch, "E11.right", {"start": v(10.26, 20.25) * mm, "end": v(10.26, -20.25) * mm});
            skSolve(sketch);
        }
        {
            var Q0;
            Q0 = qSketchRegion(id + "F21", true);
            extrude(context, id + "F22", {"entities" : qUnion([Q0]), "operationType" : NewBodyOperationType.ADD, "depth" : 2 * mm});
        }
        {
            var Q0;
            Q0=makeQuery(id+"F22.opExtrude","CAP_EDGE",EDGE,{"disambiguationData":[OSD([sQuery(id+"F21.wireOp",EDGE,"E11.left")])],"isStart":false});
            var Q1;
            Q1=makeQuery(id+"F22.opExtrude","CAP_EDGE",EDGE,{"disambiguationData":[OSD([sQuery(id+"F21.wireOp",EDGE,"E11.bottom")])],"isStart":false});
            var Q2;
            Q2=makeQuery(id+"F22.opExtrude","CAP_EDGE",EDGE,{"disambiguationData":[OSD([sQuery(id+"F21.wireOp",EDGE,"E11.right")])],"isStart":false});
            var Q3;
            Q3=makeQuery(id+"F22.opExtrude","CAP_EDGE",EDGE,{"disambiguationData":[OSD([sQuery(id+"F21.wireOp",EDGE,"E11.top")])],"isStart":false});
            fillet(context, id + "F23", {"entities" : qUnion([Q0, Q1, Q2, Q3]), "radius" : 2 * mm, "tangentPropagation" : true, "allowEdgeOverflow" : false});
        }
        {
            var Q0;
            Q0=makeQuery(id+"F23.opFillet","BLEND_EDGE",EDGE,{"blendedFrom":[makeQuery(id+"F22.opExtrude","CAP_EDGE",EDGE,{"disambiguationData":[OSD([sQuery(id+"F21.wireOp",EDGE,"E11.bottom")])],"isStart":false}),makeQuery(id+"F22.opExtrude","CAP_EDGE",EDGE,{"disambiguationData":[OSD([sQuery(id+"F21.wireOp",EDGE,"E11.left")])],"isStart":false})],"blendedInto":[]});
            var Q1;
            Q1=makeQuery(id+"F23.opFillet","BLEND_EDGE",EDGE,{"blendedFrom":[makeQuery(id+"F22.opExtrude","CAP_EDGE",EDGE,{"disambiguationData":[OSD([sQuery(id+"F21.wireOp",EDGE,"E11.top")])],"isStart":false}),makeQuery(id+"F22.opExtrude","CAP_EDGE",EDGE,{"disambiguationData":[OSD([sQuery(id+"F21.wireOp",EDGE,"E11.left")])],"isStart":false})],"blendedInto":[]});
            var Q2;
            Q2=makeQuery(id+"F23.opFillet","BLEND_EDGE",EDGE,{"blendedFrom":[makeQuery(id+"F22.opExtrude","CAP_EDGE",EDGE,{"disambiguationData":[OSD([sQuery(id+"F21.wireOp",EDGE,"E11.bottom")])],"isStart":false}),makeQuery(id+"F22.opExtrude","CAP_EDGE",EDGE,{"disambiguationData":[OSD([sQuery(id+"F21.wireOp",EDGE,"E11.right")])],"isStart":false})],"blendedInto":[]});
            var Q3;
            Q3=makeQuery(id+"F23.opFillet","BLEND_EDGE",EDGE,{"blendedFrom":[makeQuery(id+"F22.opExtrude","CAP_EDGE",EDGE,{"disambiguationData":[OSD([sQuery(id+"F21.wireOp",EDGE,"E11.top")])],"isStart":false}),makeQuery(id+"F22.opExtrude","CAP_EDGE",EDGE,{"disambiguationData":[OSD([sQuery(id+"F21.wireOp",EDGE,"E11.right")])],"isStart":false})],"blendedInto":[]});
            fillet(context, id + "F24", {"entities" : qUnion([Q0, Q1, Q2, Q3]), "radius" : 1 * mm, "tangentPropagation" : true, "allowEdgeOverflow" : false});
        }
        {
            var Q0;
            Q0=makeQuery(id+"F18.boolean.opBoolean","COPY",FACE,{"derivedFrom":makeQuery(id+"F18.opExtrude","SWEPT_FACE",FACE,{"disambiguationData":[OSD([sQuery(id+"F17.wireOp",EDGE,"E7.left")])]})});
            var sketch = newSketch(context, id + "F25", { "sketchPlane" : qUnion([Q0])});
            skCircle(sketch, "E12", {"center": v(-14.19, 66.31) * mm, "radius": 0.6 * mm});
            skCircle(sketch, "E13.0.1.0", {"center": v(-14.19, 63.31) * mm, "radius": 0.6 * mm});
            skCircle(sketch, "E13.0.2.0", {"center": v(-14.19, 60.31) * mm, "radius": 0.6 * mm});
            skCircle(sketch, "E13.0.3.0", {"center": v(-14.19, 57.31) * mm, "radius": 0.6 * mm});
            skCircle(sketch, "E13.0.4.0", {"center": v(-14.19, 54.31) * mm, "radius": 0.6 * mm});
            skCircle(sketch, "E13.1.0.0", {"center": v(-11.09, 66.31) * mm, "radius": 0.6 * mm});
            skCircle(sketch, "E13.1.1.0", {"center": v(-11.09, 63.31) * mm, "radius": 0.6 * mm});
            skCircle(sketch, "E13.1.2.0", {"center": v(-11.09, 60.31) * mm, "radius": 0.6 * mm});
            skCircle(sketch, "E13.1.3.0", {"center": v(-11.09, 57.31) * mm, "radius": 0.6 * mm});
            skCircle(sketch, "E13.1.4.0", {"center": v(-11.09, 54.31) * mm, "radius": 0.6 * mm});
            skCircle(sketch, "E13.2.0.0", {"center": v(-7.99, 66.31) * mm, "radius": 0.6 * mm});
            skCircle(sketch, "E13.2.1.0", {"center": v(-7.99, 63.31) * mm, "radius": 0.6 * mm});
            skCircle(sketch, "E13.2.2.0", {"center": v(-7.99, 60.31) * mm, "radius": 0.6 * mm});
            skCircle(sketch, "E13.2.3.0", {"center": v(-7.99, 57.31) * mm, "radius": 0.6 * mm});
            skCircle(sketch, "E13.2.4.0", {"center": v(-7.99, 54.31) * mm, "radius": 0.6 * mm});
            skCircle(sketch, "E13.3.0.0", {"center": v(-4.89, 66.31) * mm, "radius": 0.6 * mm});
            skCircle(sketch, "E13.3.1.0", {"center": v(-4.89, 63.31) * mm, "radius": 0.6 * mm});
            skCircle(sketch, "E13.3.2.0", {"center": v(-4.89, 60.31) * mm, "radius": 0.6 * mm});
            skCircle(sketch, "E13.3.3.0", {"center": v(-4.89, 57.31) * mm, "radius": 0.6 * mm});
            skCircle(sketch, "E13.3.4.0", {"center": v(-4.89, 54.31) * mm, "radius": 0.6 * mm});
            skCircle(sketch, "E13.4.0.0", {"center": v(-1.79, 66.31) * mm, "radius": 0.6 * mm});
            skCircle(sketch, "E13.4.1.0", {"center": v(-1.79, 63.31) * mm, "radius": 0.6 * mm});
            skCircle(sketch, "E13.4.2.0", {"center": v(-1.79, 60.31) * mm, "radius": 0.6 * mm});
            skCircle(sketch, "E13.4.3.0", {"center": v(-1.79, 57.31) * mm, "radius": 0.6 * mm});
            skCircle(sketch, "E13.4.4.0", {"center": v(-1.79, 54.31) * mm, "radius": 0.6 * mm});
            skCircle(sketch, "E13.5.0.0", {"center": v(1.31, 66.31) * mm, "radius": 0.6 * mm});
            skCircle(sketch, "E13.5.1.0", {"center": v(1.31, 63.31) * mm, "radius": 0.6 * mm});
            skCircle(sketch, "E13.5.2.0", {"center": v(1.31, 60.31) * mm, "radius": 0.6 * mm});
            skCircle(sketch, "E13.5.3.0", {"center": v(1.31, 57.31) * mm, "radius": 0.6 * mm});
            skCircle(sketch, "E13.5.4.0", {"center": v(1.31, 54.31) * mm, "radius": 0.6 * mm});
            skCircle(sketch, "E13.6.0.0", {"center": v(4.41, 66.31) * mm, "radius": 0.6 * mm});
            skCircle(sketch, "E13.6.1.0", {"center": v(4.41, 63.31) * mm, "radius": 0.6 * mm});
            skCircle(sketch, "E13.6.2.0", {"center": v(4.41, 60.31) * mm, "radius": 0.6 * mm});
            skCircle(sketch, "E13.6.3.0", {"center": v(4.41, 57.31) * mm, "radius": 0.6 * mm});
            skCircle(sketch, "E13.6.4.0", {"center": v(4.41, 54.31) * mm, "radius": 0.6 * mm});
            skCircle(sketch, "E13.7.0.0", {"center": v(7.51, 66.31) * mm, "radius": 0.6 * mm});
            skCircle(sketch, "E13.7.1.0", {"center": v(7.51, 63.31) * mm, "radius": 0.6 * mm});
            skCircle(sketch, "E13.7.2.0", {"center": v(7.51, 60.31) * mm, "radius": 0.6 * mm});
            skCircle(sketch, "E13.7.3.0", {"center": v(7.51, 57.31) * mm, "radius": 0.6 * mm});
            skCircle(sketch, "E13.7.4.0", {"center": v(7.51, 54.31) * mm, "radius": 0.6 * mm});
            skCircle(sketch, "E13.8.0.0", {"center": v(10.61, 66.31) * mm, "radius": 0.6 * mm});
            skCircle(sketch, "E13.8.1.0", {"center": v(10.61, 63.31) * mm, "radius": 0.6 * mm});
            skCircle(sketch, "E13.8.2.0", {"center": v(10.61, 60.31) * mm, "radius": 0.6 * mm});
            skCircle(sketch, "E13.8.3.0", {"center": v(10.61, 57.31) * mm, "radius": 0.6 * mm});
            skCircle(sketch, "E13.8.4.0", {"center": v(10.61, 54.31) * mm, "radius": 0.6 * mm});
            skCircle(sketch, "E13.9.0.0", {"center": v(13.71, 66.31) * mm, "radius": 0.6 * mm});
            skCircle(sketch, "E13.9.1.0", {"center": v(13.71, 63.31) * mm, "radius": 0.6 * mm});
            skCircle(sketch, "E13.9.2.0", {"center": v(13.71, 60.31) * mm, "radius": 0.6 * mm});
            skCircle(sketch, "E13.9.3.0", {"center": v(13.71, 57.31) * mm, "radius": 0.6 * mm});
            skCircle(sketch, "E13.9.4.0", {"center": v(13.71, 54.31) * mm, "radius": 0.6 * mm});
            skLineSegment(sketch, "E13.direction1", {"start": v(-14.19, 66.31) * mm, "end": v(-11.09, 66.31) * mm, "construction": true});
            skLineSegment(sketch, "E13.direction2", {"start": v(-14.19, 66.31) * mm, "end": v(-14.19, 63.31) * mm, "construction": true});
            skSolve(sketch);
        }
        {
            var Q0;
            Q0 = qSketchRegion(id + "F25", true);
            extrude(context, id + "F26", {"entities" : qUnion([Q0]), "operationType" : NewBodyOperationType.ADD, "depth" : 12.5 * mm});
        }
        {
            var Q0;
            Q0=makeQuery(id+"F1.opExtrude","SWEPT_FACE",FACE,{"disambiguationData":[OSD([sQuery(id+"F0.wireOp",EDGE,"E0.rect.right")])]});
            cPlane(context, id + "F27", {"entities" : qUnion([Q0]), "cplaneType" : CPlaneType.OFFSET, "offset" : 0 * mm, "width" : 150 * mm, "height" : 150 * mm});
        }
        {
            var Q0;
            Q0=makeQuery(id+"F12.opExtrude","SWEPT_FACE",FACE,{"disambiguationData":[OSD([sQuery(id+"F11.wireOp",EDGE,"E5.left")])]});
            var sketch = newSketch(context, id + "F28", { "sketchPlane" : qUnion([Q0])});
            skCircle(sketch, "E14.0.2.0", {"center": v(-15, 54.8) * mm, "radius": 0.6 * mm});
            skCircle(sketch, "E14.1.2.0", {"center": v(-12, 54.8) * mm, "radius": 0.6 * mm});
            skCircle(sketch, "E14.2.2.0", {"center": v(-9, 54.8) * mm, "radius": 0.6 * mm});
            skCircle(sketch, "E14.3.2.0", {"center": v(-6, 54.8) * mm, "radius": 0.6 * mm});
            skCircle(sketch, "E14.4.2.0", {"center": v(-3, 54.8) * mm, "radius": 0.6 * mm});
            skCircle(sketch, "E14.5.2.0", {"center": v(0, 54.8) * mm, "radius": 0.6 * mm});
            skCircle(sketch, "E14.6.2.0", {"center": v(3, 54.8) * mm, "radius": 0.6 * mm});
            skCircle(sketch, "E14.7.2.0", {"center": v(6, 54.8) * mm, "radius": 0.6 * mm});
            skCircle(sketch, "E14.8.2.0", {"center": v(9, 54.8) * mm, "radius": 0.6 * mm});
            skCircle(sketch, "E14.9.2.0", {"center": v(12, 54.8) * mm, "radius": 0.6 * mm});
            skCircle(sketch, "E14.10.2.0", {"center": v(15, 54.8) * mm, "radius": 0.6 * mm});
            skCircle(sketch, "E14.0.1.0", {"center": v(-15, 59.8) * mm, "radius": 0.6 * mm});
            skCircle(sketch, "E14.1.1.0", {"center": v(-12, 59.8) * mm, "radius": 0.6 * mm});
            skCircle(sketch, "E14.2.1.0", {"center": v(-9, 59.8) * mm, "radius": 0.6 * mm});
            skCircle(sketch, "E14.3.1.0", {"center": v(-6, 59.8) * mm, "radius": 0.6 * mm});
            skCircle(sketch, "E14.4.1.0", {"center": v(-3, 59.8) * mm, "radius": 0.6 * mm});
            skCircle(sketch, "E14.5.1.0", {"center": v(0, 59.8) * mm, "radius": 0.6 * mm});
            skCircle(sketch, "E14.6.1.0", {"center": v(3, 59.8) * mm, "radius": 0.6 * mm});
            skCircle(sketch, "E14.7.1.0", {"center": v(6, 59.8) * mm, "radius": 0.6 * mm});
            skCircle(sketch, "E14.8.1.0", {"center": v(9, 59.8) * mm, "radius": 0.6 * mm});
            skCircle(sketch, "E14.9.1.0", {"center": v(12, 59.8) * mm, "radius": 0.6 * mm});
            skCircle(sketch, "E14.10.1.0", {"center": v(15, 59.8) * mm, "radius": 0.6 * mm});
            skLineSegment(sketch, "E14.direction2", {"start": v(-15, 64.8) * mm, "end": v(-15, 59.8) * mm, "construction": true});
            skCircle(sketch, "E14.1.0.0", {"center": v(-12, 64.8) * mm, "radius": 0.6 * mm});
            skCircle(sketch, "E14.6.0.0", {"center": v(3, 64.8) * mm, "radius": 0.6 * mm});
            skCircle(sketch, "E14.9.0.0", {"center": v(12, 64.8) * mm, "radius": 0.6 * mm});
            skCircle(sketch, "E14.4.0.0", {"center": v(-3, 64.8) * mm, "radius": 0.6 * mm});
            skCircle(sketch, "E14.10.0.0", {"center": v(15, 64.8) * mm, "radius": 0.6 * mm});
            skCircle(sketch, "E15", {"center": v(-15, 64.8) * mm, "radius": 0.6 * mm});
            skCircle(sketch, "E14.2.0.0", {"center": v(-9, 64.8) * mm, "radius": 0.6 * mm});
            skCircle(sketch, "E14.3.0.0", {"center": v(-6, 64.8) * mm, "radius": 0.6 * mm});
            skCircle(sketch, "E14.5.0.0", {"center": v(0, 64.8) * mm, "radius": 0.6 * mm});
            skCircle(sketch, "E14.7.0.0", {"center": v(6, 64.8) * mm, "radius": 0.6 * mm});
            skCircle(sketch, "E14.8.0.0", {"center": v(9, 64.8) * mm, "radius": 0.6 * mm});
            skLineSegment(sketch, "E14.direction1", {"start": v(-15, 64.8) * mm, "end": v(-12, 64.8) * mm, "construction": true});
            skSolve(sketch);
        }
        {
            var Q0;
            Q0 = qSketchRegion(id + "F28", true);
            var Q1;
            Q1=qCreatedBy(id+"F27.planeOp",FACE);
            extrude(context, id + "F29", {"entities" : qUnion([Q0]), "operationType" : NewBodyOperationType.ADD, "endBound" : BoundingType.UP_TO_SURFACE, "endBoundEntityFace" : qUnion([Q1]), "depth" : 25 * mm});
        }
        {
            var Q0;
            Q0=makeQuery(id+"F14.opExtrude","SWEPT_FACE",FACE,{"disambiguationData":[OSD([sQuery(id+"F13.wireOp",EDGE,"E6.left")])]});
            var sketch = newSketch(context, id + "F30", { "sketchPlane" : qUnion([Q0])});
            skLineSegment(sketch, "E16.top", {"start": v(-19, 56.75) * mm, "end": v(19, 56.75) * mm});
            skLineSegment(sketch, "E16.bottom", {"start": v(-19, 57.25) * mm, "end": v(19, 57.25) * mm});
            skLineSegment(sketch, "E17.direction2", {"start": v(-19, 56.75) * mm, "end": v(-19, 61.75) * mm, "construction": true});
            skLineSegment(sketch, "E17.0.1.0", {"start": v(-19, 61.75) * mm, "end": v(19, 61.75) * mm});
            skLineSegment(sketch, "E17.0.1.1", {"start": v(-19, 62.25) * mm, "end": v(19, 62.25) * mm});
            skLineSegment(sketch, "E17.0.2.0", {"start": v(-19, 66.75) * mm, "end": v(19, 66.75) * mm});
            skLineSegment(sketch, "E17.0.2.1", {"start": v(-19, 67.25) * mm, "end": v(19, 67.25) * mm});
            skLineSegment(sketch, "E17.direction1", {"start": v(-19, 56.75) * mm, "end": v(-9.61, 56.75) * mm, "construction": true});
            skLineSegment(sketch, "E16.right", {"start": v(19, 57.25) * mm, "end": v(19, 56.75) * mm});
            skLineSegment(sketch, "E17.0.2.3", {"start": v(-19, 67.25) * mm, "end": v(-19, 66.75) * mm});
            skLineSegment(sketch, "E17.0.1.3", {"start": v(-19, 62.25) * mm, "end": v(-19, 61.75) * mm});
            skLineSegment(sketch, "E17.0.1.2", {"start": v(19, 62.25) * mm, "end": v(19, 61.75) * mm});
            skLineSegment(sketch, "E17.0.2.2", {"start": v(19, 67.25) * mm, "end": v(19, 66.75) * mm});
            skLineSegment(sketch, "E16.left", {"start": v(-19, 57.25) * mm, "end": v(-19, 56.75) * mm});
            skSolve(sketch);
        }
        {
            var Q0;
            Q0 = qSketchRegion(id + "F30", true);
            var Q1;
            Q1=qCreatedBy(id+"F27.planeOp",FACE);
            extrude(context, id + "F31", {"entities" : qUnion([Q0]), "operationType" : NewBodyOperationType.ADD, "endBound" : BoundingType.UP_TO_SURFACE, "endBoundEntityFace" : qUnion([Q1]), "depth" : 25 * mm});
        }
    });
